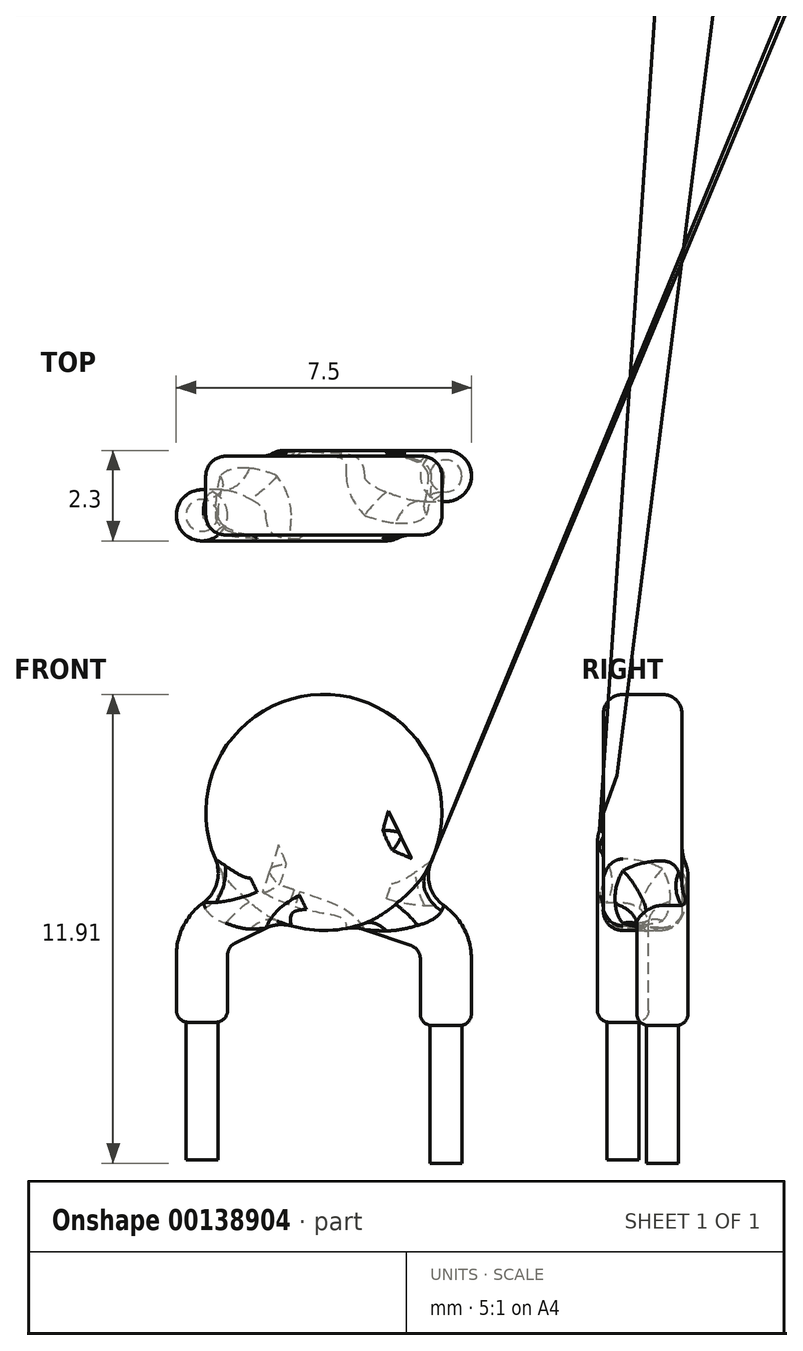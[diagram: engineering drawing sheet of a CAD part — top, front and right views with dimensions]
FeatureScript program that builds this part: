
annotation { "Feature Type Name" : "Feature", "Feature Type Description" : "" }
export const myFeature = defineFeature(function(context is Context, id is Id, definition is map)
    precondition{}
    {
        {
            var Q0;
            Q0=qCreatedBy(makeId("Front.planeOp"),FACE);
            var sketch = newSketch(context, id + "F0", { "sketchPlane" : qUnion([Q0])});
            skCircle(sketch, "E0", {"center": v(0, 0) * mm, "radius": 3 * mm});
            skSolve(sketch);
        }
        {
            var Q0;
            Q0=makeQuery(id+"F0.imprint","IMPRINT",FACE,{"disambiguationData":[TD([[makeQuery(id+"F0.imprint","IMPRINT",EDGE,{"derivedFrom":sQuery(id+"F0.wireOp",EDGE,"E0")}),1.0]])]});
            extrude(context, id + "F1", {"entities" : qUnion([Q0]), "endBound" : BoundingType.SYMMETRIC, "depth" : 2 * mm});
        }
        {
            var Q0;
            Q0=makeQuery(id+"F1.opExtrude","CAP_EDGE",EDGE,{"disambiguationData":[OSD([sQuery(id+"F0.wireOp",EDGE,"E0")])],"isStart":false});
            var Q1;
            Q1=makeQuery(id+"F1.opExtrude","CAP_EDGE",EDGE,{"disambiguationData":[OSD([sQuery(id+"F0.wireOp",EDGE,"E0")])],"isStart":true});
            fillet(context, id + "F2", {"entities" : qUnion([Q0, Q1]), "radius" : 0.5 * mm, "tangentPropagation" : true, "allowEdgeOverflow" : false});
        }
        {
            var Q0;
            Q0=makeQuery(id+"F1.opExtrude","CAP_FACE",FACE,{"disambiguationData":[OSD([sQuery(id+"F0.wireOp",EDGE,"E0")])],"isStart":false});
            cPlane(context, id + "F3", {"entities" : qUnion([Q0]), "cplaneType" : CPlaneType.OFFSET, "offset" : 0.5 * mm, "oppositeDirection" : true, "width" : 150 * mm, "height" : 150 * mm});
        }
        {
            var Q0;
            Q0=makeQuery(id+"F1.opExtrude","CAP_FACE",FACE,{"disambiguationData":[OSD([sQuery(id+"F0.wireOp",EDGE,"E0")])],"isStart":true});
            cPlane(context, id + "F4", {"entities" : qUnion([Q0]), "cplaneType" : CPlaneType.OFFSET, "offset" : 0.5 * mm, "oppositeDirection" : true, "width" : 150 * mm, "height" : 150 * mm});
        }
        {
            var Q0;
            Q0=qCreatedBy(id+"F4.planeOp",FACE);
            var sketch = newSketch(context, id + "F5", { "sketchPlane" : qUnion([Q0])});
            skLineSegment(sketch, "E1", {"start": v(-3.1, -5.41) * mm, "end": v(-3.1, -3.71) * mm});
            skLineSegment(sketch, "E2", {"start": v(-2.42, -2.77) * mm, "end": v(1.37, -1.46) * mm});
            skPoint(sketch, "E3.visualSharp", {"position": v(-3.1, -3) * mm});
            skArc(sketch, "E4.filletArc", {"start": v(-2.42, -2.77) * mm, "mid": v(-2.91, -3.13) * mm, "end": v(-3.1, -3.71) * mm});
            skLineSegment(sketch, "E5", {"start": v(-3.1, -5.41) * mm, "end": v(-3.1, -8.91) * mm});
            skSolve(sketch);
        }
        {
            var Q0;
            Q0=qCreatedBy(id+"F3.planeOp",FACE);
            var sketch = newSketch(context, id + "F6", { "sketchPlane" : qUnion([Q0])});
            skLineSegment(sketch, "E6", {"start": v(-3.1, -5.33) * mm, "end": v(-3.1, -3.63) * mm});
            skLineSegment(sketch, "E7", {"start": v(-2.53, -2.73) * mm, "end": v(1.93, -0.56) * mm});
            skPoint(sketch, "E8.visualSharp", {"position": v(-3.1, -3) * mm});
            skArc(sketch, "E8.filletArc", {"start": v(-2.53, -2.73) * mm, "mid": v(-2.94, -3.1) * mm, "end": v(-3.1, -3.63) * mm});
            skLineSegment(sketch, "E9", {"start": v(-3.1, -5.33) * mm, "end": v(-3.1, -8.83) * mm});
            skSolve(sketch);
        }
        {
            var Q0;
            Q0=sQuery(id+"F6.wireOp",VERTEX,"E9.start");
            var Q1;
            Q1=qCreatedBy(makeId("Top.planeOp"),FACE);
            cPlane(context, id + "F7", {"entities" : qUnion([Q0, Q1]), "cplaneType" : CPlaneType.PLANE_POINT, "offset" : 0 * mm, "width" : 150 * mm, "height" : 150 * mm});
        }
        {
            var Q0;
            Q0=qCreatedBy(id+"F7.planeOp",FACE);
            var sketch = newSketch(context, id + "F8", { "sketchPlane" : qUnion([Q0])});
            skCircle(sketch, "E10", {"center": v(-3.1, -0.5) * mm, "radius": 0.65 * mm});
            skSolve(sketch);
        }
        {
            var Q0;
            Q0=makeQuery(id+"F8.imprint","IMPRINT",FACE,{"disambiguationData":[TD([[makeQuery(id+"F8.imprint","IMPRINT",EDGE,{"derivedFrom":sQuery(id+"F8.wireOp",EDGE,"E10")}),1.0]])]});
            var Q1;
            Q1=sQuery(id+"F6.wireOp",EDGE,"E6");
            var Q2;
            Q2=sQuery(id+"F6.wireOp",EDGE,"E8.filletArc");
            var Q3;
            Q3=sQuery(id+"F6.wireOp",EDGE,"E7");
            sweep(context, id + "F9", {"operationType" : NewBodyOperationType.ADD, "profiles" : qUnion([Q0]), "path" : qUnion([Q1, Q2, Q3])});
        }
        {
            var Q0;
            Q0=makeQuery(id+"F9.boolean.opBoolean","INTERSECT",EDGE,{"disambiguationData":[OD(1.0)],"derivedFrom":[makeQuery(id+"F1.opExtrude","CAP_FACE",FACE,{"disambiguationData":[OSD([sQuery(id+"F0.wireOp",EDGE,"E0")])],"isStart":false}),makeQuery(id+"F9.opSweep","SWEPT_FACE",FACE,{"disambiguationData":[OSD([sQuery(id+"F6.wireOp",EDGE,"E7"),sQuery(id+"F8.wireOp",EDGE,"E10")])]})]});
            fillet(context, id + "F10", {"entities" : qUnion([Q0]), "radius" : 0.92 * mm, "tangentPropagation" : true, "allowEdgeOverflow" : false});
        }
        {
            var Q0;
            Q0=sQuery(id+"F5.wireOp",VERTEX,"E5.start");
            var Q1;
            Q1=qCreatedBy(makeId("Top.planeOp"),FACE);
            cPlane(context, id + "F11", {"entities" : qUnion([Q0, Q1]), "cplaneType" : CPlaneType.PLANE_POINT, "offset" : 25 * mm, "width" : 150 * mm, "height" : 150 * mm});
        }
        {
            var Q0;
            Q0=qCreatedBy(id+"F11.planeOp",FACE);
            var sketch = newSketch(context, id + "F12", { "sketchPlane" : qUnion([Q0])});
            skCircle(sketch, "E11", {"center": v(3.1, 0.5) * mm, "radius": 0.65 * mm});
            skSolve(sketch);
        }
        {
            var Q0;
            Q0=makeQuery(id+"F12.imprint","IMPRINT",FACE,{"disambiguationData":[TD([[makeQuery(id+"F12.imprint","IMPRINT",EDGE,{"derivedFrom":sQuery(id+"F12.wireOp",EDGE,"E11")}),1.0]])]});
            var Q1;
            Q1=sQuery(id+"F5.wireOp",EDGE,"E1");
            var Q2;
            Q2=sQuery(id+"F5.wireOp",EDGE,"E4.filletArc");
            var Q3;
            Q3=sQuery(id+"F5.wireOp",EDGE,"E2");
            sweep(context, id + "F13", {"operationType" : NewBodyOperationType.ADD, "profiles" : qUnion([Q0]), "path" : qUnion([Q1, Q2, Q3])});
        }
        {
            var Q0;
            Q0=makeQuery(id+"F13.boolean.opBoolean","INTERSECT",EDGE,{"disambiguationData":[OD(0.0)],"derivedFrom":[makeQuery(id+"F1.opExtrude","CAP_FACE",FACE,{"disambiguationData":[OSD([sQuery(id+"F0.wireOp",EDGE,"E0")])],"isStart":true}),makeQuery(id+"F13.opSweep","SWEPT_FACE",FACE,{"disambiguationData":[OSD([sQuery(id+"F5.wireOp",EDGE,"E2"),sQuery(id+"F12.wireOp",EDGE,"E11")])]})]});
            fillet(context, id + "F14", {"entities" : qUnion([Q0]), "radius" : 0.92 * mm, "tangentPropagation" : true, "allowEdgeOverflow" : false});
        }
        {
            var Q0;
            {var subQ0=sQuery(id+"F12.wireOp",EDGE,"E11");Q0=makeQuery(id+"F14.opFillet","BLEND_EDGE",EDGE,{"blendedFrom":[makeQuery(id+"F13.boolean.opBoolean","INTERSECT",EDGE,{"disambiguationData":[OD(0.0)],"derivedFrom":[makeQuery(id+"F1.opExtrude","CAP_FACE",FACE,{"disambiguationData":[OSD([sQuery(id+"F0.wireOp",EDGE,"E0")])],"isStart":true}),makeQuery(id+"F13.opSweep","SWEPT_FACE",FACE,{"disambiguationData":[OSD([sQuery(id+"F5.wireOp",EDGE,"E2"),subQ0])]})]}),makeQuery(id+"F13.opSweep","CAP_FACE",FACE,{"disambiguationData":[OSD([sQuery(id+"F5.wireOp",VERTEX,"E2.end"),subQ0])],"isStart":false})],"blendedInto":[makeQuery(id+"F13.opSweep","CAP_FACE",FACE,{"disambiguationData":[OSD([sQuery(id+"F5.wireOp",VERTEX,"E2.end"),subQ0])],"isStart":false})]});}
            var Q1;
            {var subQ0=sQuery(id+"F12.wireOp",EDGE,"E11");Q1=makeQuery(id+"F14.opFillet","BLEND_EDGE",EDGE,{"blendedFrom":[makeQuery(id+"F13.boolean.opBoolean","INTERSECT",EDGE,{"disambiguationData":[OD(1.0)],"derivedFrom":[makeQuery(id+"F1.opExtrude","CAP_FACE",FACE,{"disambiguationData":[OSD([sQuery(id+"F0.wireOp",EDGE,"E0")])],"isStart":true}),makeQuery(id+"F13.opSweep","SWEPT_FACE",FACE,{"disambiguationData":[OSD([sQuery(id+"F5.wireOp",EDGE,"E2"),subQ0])]})]}),makeQuery(id+"F13.opSweep","CAP_FACE",FACE,{"disambiguationData":[OSD([sQuery(id+"F5.wireOp",VERTEX,"E2.end"),subQ0])],"isStart":false})],"blendedInto":[makeQuery(id+"F13.opSweep","CAP_FACE",FACE,{"disambiguationData":[OSD([sQuery(id+"F5.wireOp",VERTEX,"E2.end"),subQ0])],"isStart":false})]});}
            var Q2;
            Q2=makeQuery(id+"F13.opSweep","CAP_EDGE",EDGE,{"disambiguationData":[OSD([sQuery(id+"F5.wireOp",VERTEX,"E2.end"),sQuery(id+"F12.wireOp",EDGE,"E11")])],"isStart":false});
            fillet(context, id + "F15", {"entities" : qUnion([Q0, Q1, Q2]), "radius" : 0.5 * mm, "tangentPropagation" : true, "allowEdgeOverflow" : false});
        }
        {
            var Q0;
            Q0=qCreatedBy(id+"F11.planeOp",FACE);
            var Q1;
            Q1=sQuery(id+"F6.wireOp",VERTEX,"E9.end");
            cPlane(context, id + "F16", {"entities" : qUnion([Q0, Q1]), "cplaneType" : CPlaneType.PLANE_POINT, "offset" : 25 * mm, "width" : 150 * mm, "height" : 150 * mm});
        }
        {
            var Q0;
            Q0=qCreatedBy(id+"F16.planeOp",FACE);
            var sketch = newSketch(context, id + "F17", { "sketchPlane" : qUnion([Q0])});
            skCircle(sketch, "E12", {"center": v(-3.1, -0.5) * mm, "radius": 0.4 * mm});
            skCircle(sketch, "E13", {"center": v(3.1, 0.5) * mm, "radius": 0.4 * mm});
            skSolve(sketch);
        }
        {
            var Q0;
            Q0=makeQuery(id+"F17.imprint","IMPRINT",FACE,{"disambiguationData":[TD([[makeQuery(id+"F17.imprint","IMPRINT",EDGE,{"derivedFrom":sQuery(id+"F17.wireOp",EDGE,"E12")}),1.0]])]});
            var Q1;
            Q1=sQuery(id+"F6.wireOp",EDGE,"E9");
            sweep(context, id + "F18", {"profiles" : qUnion([Q0]), "path" : qUnion([Q1])});
        }
        {
            var Q0;
            Q0=makeQuery(id+"F17.imprint","IMPRINT",FACE,{"disambiguationData":[TD([[makeQuery(id+"F17.imprint","IMPRINT",EDGE,{"derivedFrom":sQuery(id+"F17.wireOp",EDGE,"E13")}),1.0]])]});
            var Q1;
            Q1=sQuery(id+"F5.wireOp",EDGE,"E5");
            sweep(context, id + "F19", {"profiles" : qUnion([Q0]), "path" : qUnion([Q1])});
        }
        {
            var Q0;
            Q0=makeQuery(id+"F9.opSweep","CAP_EDGE",EDGE,{"disambiguationData":[OSD([sQuery(id+"F6.wireOp",VERTEX,"E6.start"),sQuery(id+"F8.wireOp",EDGE,"E10")])],"isStart":true});
            var Q1;
            Q1=makeQuery(id+"F13.opSweep","CAP_EDGE",EDGE,{"disambiguationData":[OSD([sQuery(id+"F5.wireOp",VERTEX,"E1.start"),sQuery(id+"F12.wireOp",EDGE,"E11")])],"isStart":true});
            fillet(context, id + "F20", {"entities" : qUnion([Q0, Q1]), "radius" : 0.3 * mm, "tangentPropagation" : true, "allowEdgeOverflow" : false});
        }
        {
            var Q0;
            {var subQ0=sQuery(id+"F8.wireOp",EDGE,"E10");Q0=makeQuery(id+"F10.opFillet","BLEND_EDGE",EDGE,{"blendedFrom":[makeQuery(id+"F9.boolean.opBoolean","INTERSECT",EDGE,{"disambiguationData":[OD(1.0)],"derivedFrom":[makeQuery(id+"F1.opExtrude","CAP_FACE",FACE,{"disambiguationData":[OSD([sQuery(id+"F0.wireOp",EDGE,"E0")])],"isStart":false}),makeQuery(id+"F9.opSweep","SWEPT_FACE",FACE,{"disambiguationData":[OSD([sQuery(id+"F6.wireOp",EDGE,"E7"),subQ0])]})]}),makeQuery(id+"F9.opSweep","CAP_FACE",FACE,{"disambiguationData":[OSD([sQuery(id+"F6.wireOp",VERTEX,"E7.end"),subQ0])],"isStart":false})],"blendedInto":[makeQuery(id+"F9.opSweep","CAP_FACE",FACE,{"disambiguationData":[OSD([sQuery(id+"F6.wireOp",VERTEX,"E7.end"),subQ0])],"isStart":false})]});}
            var Q1;
            Q1=makeQuery(id+"F9.opSweep","CAP_EDGE",EDGE,{"disambiguationData":[OSD([sQuery(id+"F6.wireOp",VERTEX,"E7.end"),sQuery(id+"F8.wireOp",EDGE,"E10")])],"isStart":false});
            var Q2;
            {var subQ0=sQuery(id+"F8.wireOp",EDGE,"E10");Q2=makeQuery(id+"F10.opFillet","BLEND_EDGE",EDGE,{"blendedFrom":[makeQuery(id+"F9.boolean.opBoolean","INTERSECT",EDGE,{"disambiguationData":[OD(0.0)],"derivedFrom":[makeQuery(id+"F1.opExtrude","CAP_FACE",FACE,{"disambiguationData":[OSD([sQuery(id+"F0.wireOp",EDGE,"E0")])],"isStart":false}),makeQuery(id+"F9.opSweep","SWEPT_FACE",FACE,{"disambiguationData":[OSD([sQuery(id+"F6.wireOp",EDGE,"E7"),subQ0])]})]}),makeQuery(id+"F9.opSweep","CAP_FACE",FACE,{"disambiguationData":[OSD([sQuery(id+"F6.wireOp",VERTEX,"E7.end"),subQ0])],"isStart":false})],"blendedInto":[makeQuery(id+"F9.opSweep","CAP_FACE",FACE,{"disambiguationData":[OSD([sQuery(id+"F6.wireOp",VERTEX,"E7.end"),subQ0])],"isStart":false})]});}
            fillet(context, id + "F21", {"entities" : qUnion([Q0, Q1, Q2]), "radius" : 0.5 * mm, "tangentPropagation" : true, "allowEdgeOverflow" : false});
        }
    });
